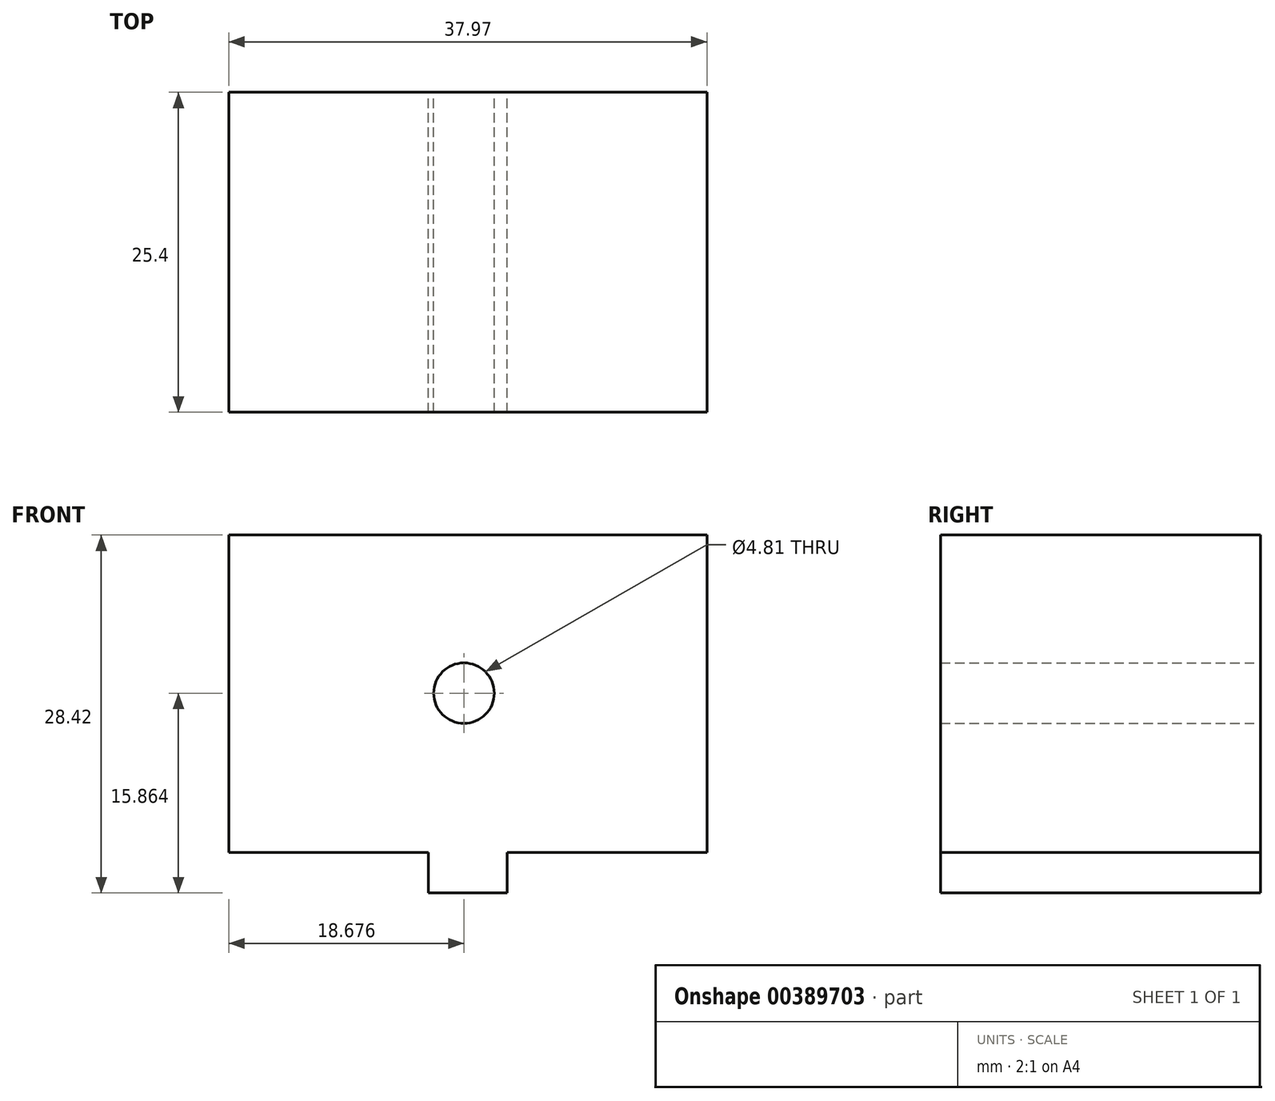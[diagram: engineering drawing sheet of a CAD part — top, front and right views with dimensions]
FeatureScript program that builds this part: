
annotation { "Feature Type Name" : "Feature", "Feature Type Description" : "" }
export const myFeature = defineFeature(function(context is Context, id is Id, definition is map)
    precondition{}
    {
        {
            var Q0;
            Q0=qCreatedBy(makeId("Front.planeOp"),FACE);
            var sketch = newSketch(context, id + "F0", { "sketchPlane" : qUnion([Q0])});
            skLineSegment(sketch, "E0", {"start": v(-20.59, 12.97) * mm, "end": v(17.38, 12.97) * mm});
            skLineSegment(sketch, "E1", {"start": v(17.38, 12.97) * mm, "end": v(17.38, -12.22) * mm});
            skLineSegment(sketch, "E2", {"start": v(17.38, -12.22) * mm, "end": v(1.52, -12.22) * mm});
            skLineSegment(sketch, "E3", {"start": v(1.52, -12.22) * mm, "end": v(1.52, -15.45) * mm});
            skLineSegment(sketch, "E4", {"start": v(1.52, -15.45) * mm, "end": v(-4.73, -15.45) * mm});
            skLineSegment(sketch, "E5", {"start": v(-4.73, -15.45) * mm, "end": v(-4.73, -12.22) * mm});
            skLineSegment(sketch, "E6", {"start": v(-4.73, -12.22) * mm, "end": v(-20.59, -12.22) * mm});
            skLineSegment(sketch, "E7", {"start": v(-20.59, -12.22) * mm, "end": v(-20.59, 12.97) * mm});
            skCircle(sketch, "E8", {"center": v(-1.91, 0.41) * mm, "radius": 2.4 * mm});
            skSolve(sketch);
        }
        {
            var Q0;
            Q0 = qSketchRegion(id + "F0", true);
            extrude(context, id + "F1", {"entities" : qUnion([Q0]), "depth" : 25.4 * mm});
        }
    });
